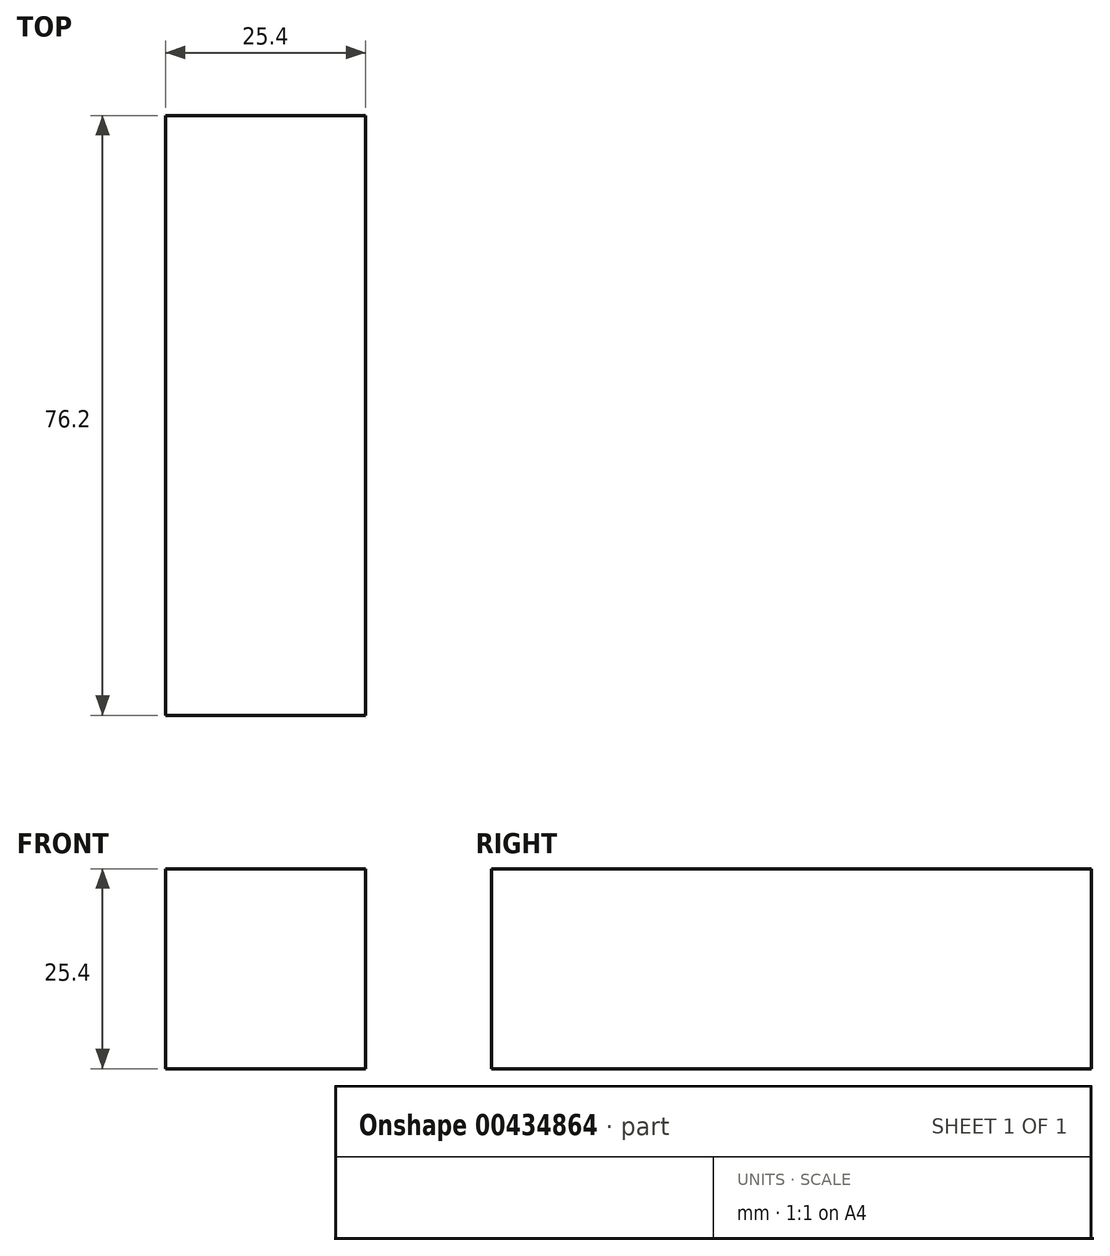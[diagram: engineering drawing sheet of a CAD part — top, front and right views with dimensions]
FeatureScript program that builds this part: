
annotation { "Feature Type Name" : "Feature", "Feature Type Description" : "" }
export const myFeature = defineFeature(function(context is Context, id is Id, definition is map)
    precondition{}
    {
        {
            var Q0;
            Q0=qCreatedBy(makeId("Front.planeOp"),FACE);
            var sketch = newSketch(context, id + "F0", { "sketchPlane" : qUnion([Q0])});
            skLineSegment(sketch, "E0.bottom", {"start": v(-3.25, 32.47) * mm, "end": v(22.15, 32.47) * mm});
            skLineSegment(sketch, "E0.top", {"start": v(-3.25, 7.07) * mm, "end": v(22.15, 7.07) * mm});
            skLineSegment(sketch, "E0.left", {"start": v(-3.25, 32.47) * mm, "end": v(-3.25, 7.07) * mm});
            skLineSegment(sketch, "E0.right", {"start": v(22.15, 32.47) * mm, "end": v(22.15, 7.07) * mm});
            skSolve(sketch);
        }
        {
            var Q0;
            Q0 = qSketchRegion(id + "F0", true);
            extrude(context, id + "F1", {"entities" : qUnion([Q0]), "depth" : 76.2 * mm});
        }
    });
